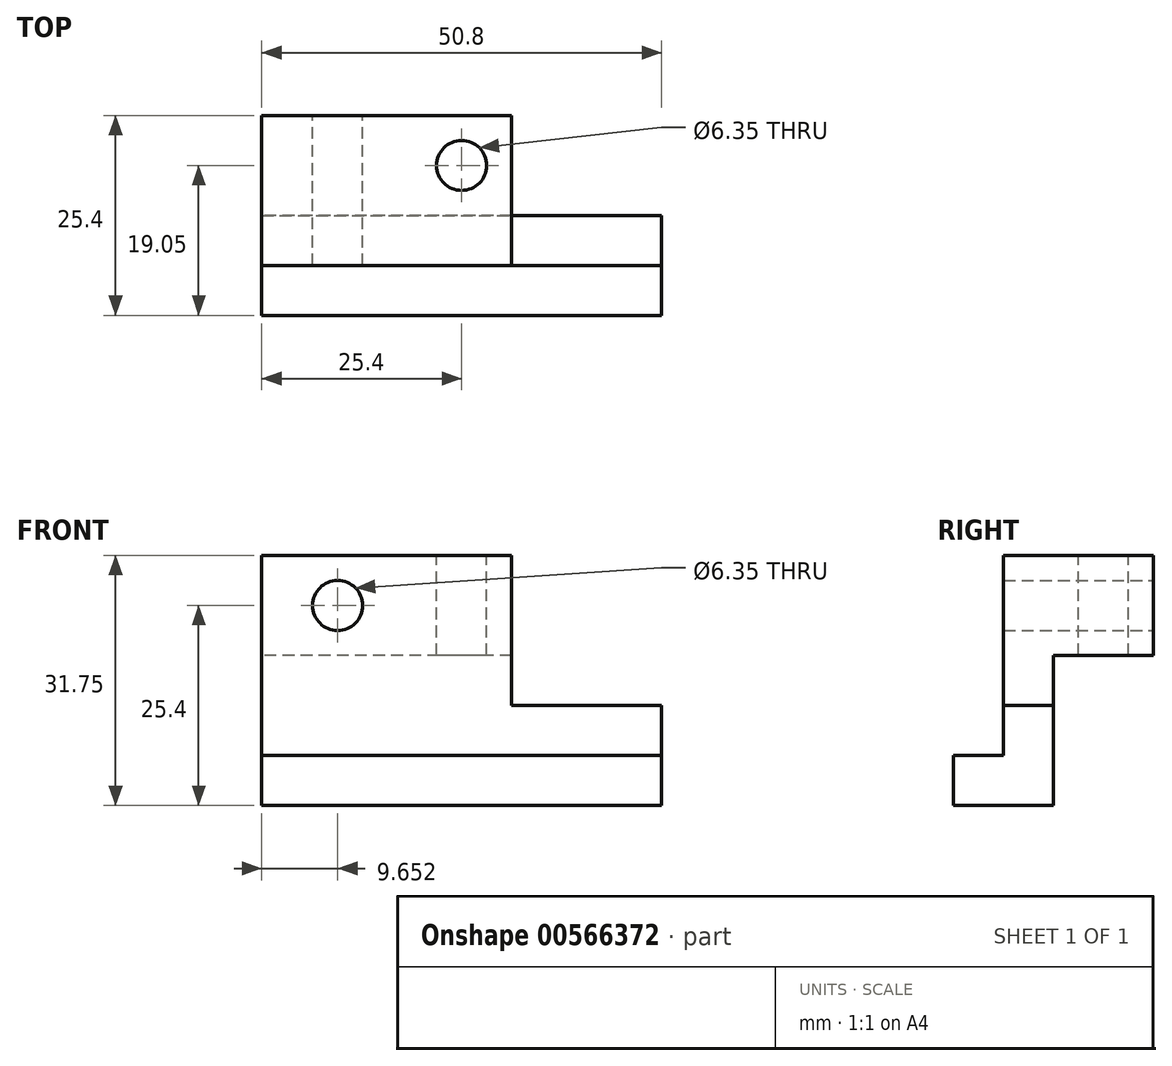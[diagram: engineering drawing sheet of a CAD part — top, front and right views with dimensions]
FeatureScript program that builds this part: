
annotation { "Feature Type Name" : "Feature", "Feature Type Description" : "" }
export const myFeature = defineFeature(function(context is Context, id is Id, definition is map)
    precondition{}
    {
        {
            var Q0;
            Q0=qCreatedBy(makeId("Front.planeOp"),FACE);
            var sketch = newSketch(context, id + "F0", { "sketchPlane" : qUnion([Q0])});
            skLineSegment(sketch, "E0", {"start": v(0, 0) * mm, "end": v(19.05, 0) * mm});
            skLineSegment(sketch, "E1", {"start": v(0, 19.05) * mm, "end": v(-31.75, 19.05) * mm});
            skLineSegment(sketch, "E2", {"start": v(-31.75, 19.05) * mm, "end": v(-31.75, -12.7) * mm});
            skLineSegment(sketch, "E3", {"start": v(19.05, 0) * mm, "end": v(19.05, -12.7) * mm});
            skLineSegment(sketch, "E4", {"start": v(-31.75, -12.7) * mm, "end": v(19.05, -12.7) * mm});
            skLineSegment(sketch, "E5", {"start": v(0, 19.05) * mm, "end": v(0, 0) * mm});
            skCircle(sketch, "E6", {"center": v(-22.1, 12.7) * mm, "radius": 3.18 * mm});
            skSolve(sketch);
        }
        {
            var Q0;
            Q0 = qSketchRegion(id + "F0", true);
            extrude(context, id + "F1", {"entities" : qUnion([Q0]), "depth" : 6.35 * mm, "offsetDistance" : 25.4 * mm});
        }
        {
            var Q0;
            Q0=makeQuery(id+"F1.opExtrude","CAP_FACE",FACE,{"disambiguationData":[OSD([sQuery(id+"F0.wireOp",EDGE,"E0"),sQuery(id+"F0.wireOp",EDGE,"E1"),sQuery(id+"F0.wireOp",EDGE,"E2"),sQuery(id+"F0.wireOp",EDGE,"E3"),sQuery(id+"F0.wireOp",EDGE,"E4"),sQuery(id+"F0.wireOp",EDGE,"E5"),sQuery(id+"F0.wireOp",EDGE,"E6")])],"isStart":false});
            var sketch = newSketch(context, id + "F2", { "sketchPlane" : qUnion([Q0])});
            skLineSegment(sketch, "E7", {"start": v(0, -6.35) * mm, "end": v(19.05, -6.35) * mm});
            skLineSegment(sketch, "E8", {"start": v(19.05, -6.35) * mm, "end": v(-31.75, -6.35) * mm});
            skLineSegment(sketch, "E9", {"start": v(-31.75, -6.35) * mm, "end": v(-31.75, -12.7) * mm});
            skLineSegment(sketch, "E10", {"start": v(-31.75, -12.7) * mm, "end": v(0, -12.7) * mm});
            skLineSegment(sketch, "E11", {"start": v(0, -12.7) * mm, "end": v(19.05, -12.7) * mm});
            skLineSegment(sketch, "E12", {"start": v(19.05, -12.7) * mm, "end": v(19.05, -6.35) * mm});
            skPoint(sketch, "E13.orphan", {"position": v(0, 0) * mm});
            skSolve(sketch);
        }
        {
            var Q0;
            Q0 = qSketchRegion(id + "F2", true);
            extrude(context, id + "F3", {"entities" : qUnion([Q0]), "operationType" : NewBodyOperationType.ADD, "depth" : 6.35 * mm, "offsetDistance" : 25.4 * mm});
        }
        {
            var Q0;
            Q0=makeQuery(id+"F1.opExtrude","CAP_FACE",FACE,{"disambiguationData":[OSD([sQuery(id+"F0.wireOp",EDGE,"E0"),sQuery(id+"F0.wireOp",EDGE,"E1"),sQuery(id+"F0.wireOp",EDGE,"E2"),sQuery(id+"F0.wireOp",EDGE,"E3"),sQuery(id+"F0.wireOp",EDGE,"E4"),sQuery(id+"F0.wireOp",EDGE,"E5"),sQuery(id+"F0.wireOp",EDGE,"E6")])],"isStart":true});
            var sketch = newSketch(context, id + "F4", { "sketchPlane" : qUnion([Q0])});
            skLineSegment(sketch, "E14.bottom", {"start": v(0, 19.05) * mm, "end": v(31.75, 19.05) * mm});
            skLineSegment(sketch, "E14.top", {"start": v(0, 6.35) * mm, "end": v(31.75, 6.35) * mm});
            skLineSegment(sketch, "E14.left", {"start": v(0, 19.05) * mm, "end": v(0, 6.35) * mm});
            skLineSegment(sketch, "E14.right", {"start": v(31.75, 19.05) * mm, "end": v(31.75, 6.35) * mm});
            skSolve(sketch);
        }
        {
            var Q0;
            Q0=makeQuery(id+"F4.imprint","IMPRINT",FACE,{"disambiguationData":[TD([[makeQuery(id+"F4.imprint","IMPRINT",EDGE,{"derivedFrom":sQuery(id+"F4.wireOp",EDGE,"E14.bottom")}),-1.0]])]});
            extrude(context, id + "F5", {"entities" : qUnion([Q0]), "operationType" : NewBodyOperationType.ADD, "depth" : 12.7 * mm, "offsetDistance" : 25.4 * mm});
        }
        {
            var Q0;
            Q0=makeQuery(id+"F5.boolean.opBoolean","MERGE",FACE,{"derivedFrom":[makeQuery(id+"F1.opExtrude","SWEPT_FACE",FACE,{"disambiguationData":[OSD([sQuery(id+"F0.wireOp",EDGE,"E1")])]}),makeQuery(id+"F5.opExtrude","SWEPT_FACE",FACE,{"disambiguationData":[OSD([sQuery(id+"F4.wireOp",EDGE,"E14.bottom")])]})]});
            var sketch = newSketch(context, id + "F6", { "sketchPlane" : qUnion([Q0])});
            skLineSegment(sketch, "E15.bottom", {"start": v(0, 12.7) * mm, "end": v(-6.35, 12.7) * mm, "construction": true});
            skLineSegment(sketch, "E15.top", {"start": v(0, 6.35) * mm, "end": v(-6.35, 6.35) * mm, "construction": true});
            skLineSegment(sketch, "E15.left", {"start": v(0, 12.7) * mm, "end": v(0, 6.35) * mm, "construction": true});
            skLineSegment(sketch, "E15.right", {"start": v(-6.35, 12.7) * mm, "end": v(-6.35, 6.35) * mm, "construction": true});
            skCircle(sketch, "E16", {"center": v(-6.35, 6.35) * mm, "radius": 3.18 * mm});
            skSolve(sketch);
        }
        {
            var Q0;
            Q0=makeQuery(id+"F6.imprint","IMPRINT",FACE,{"disambiguationData":[TD([[makeQuery(id+"F6.imprint","IMPRINT",EDGE,{"derivedFrom":sQuery(id+"F6.wireOp",EDGE,"E16")}),1.0]])]});
            extrude(context, id + "F7", {"entities" : qUnion([Q0]), "operationType" : NewBodyOperationType.REMOVE, "oppositeDirection" : true, "depth" : 25.4 * mm, "offsetDistance" : 25.4 * mm});
        }
    });
